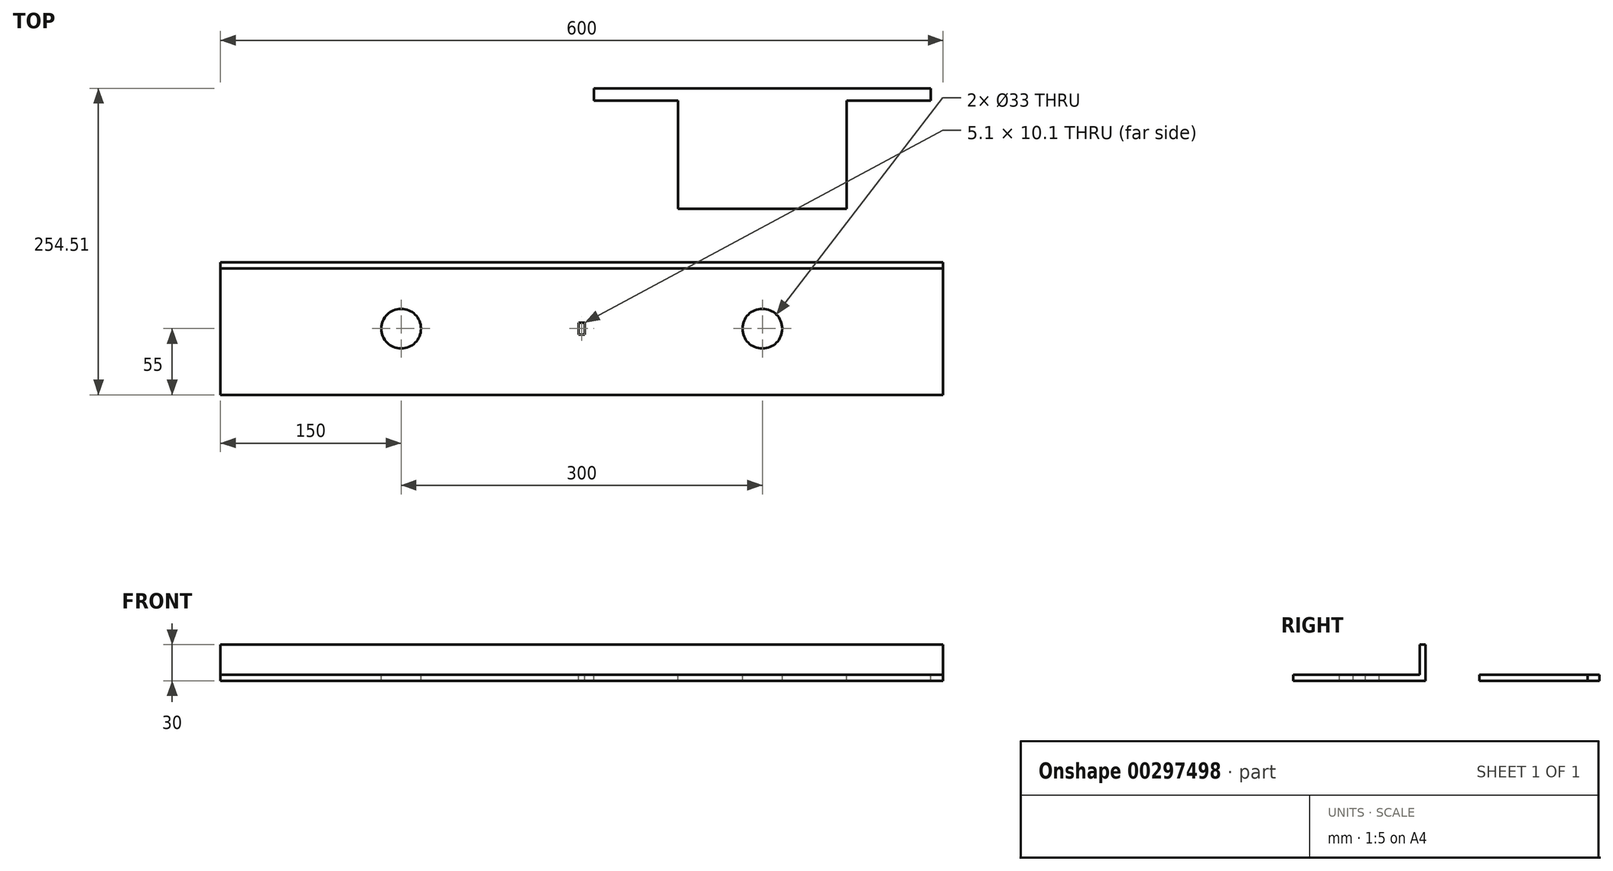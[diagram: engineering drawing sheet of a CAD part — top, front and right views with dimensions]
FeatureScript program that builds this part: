
annotation { "Feature Type Name" : "Feature", "Feature Type Description" : "" }
export const myFeature = defineFeature(function(context is Context, id is Id, definition is map)
    precondition{}
    {
        {
            var Q0;
            Q0=qCreatedBy(makeId("Top.planeOp"),FACE);
            var sketch = newSketch(context, id + "F0", { "sketchPlane" : qUnion([Q0])});
            skPoint(sketch, "E0", {"position": v(0, -50) * mm});
            skLineSegment(sketch, "E1.bottom", {"start": v(2.55, -55.05) * mm, "end": v(-2.55, -55.05) * mm});
            skLineSegment(sketch, "E1.top", {"start": v(2.55, -44.95) * mm, "end": v(-2.55, -44.95) * mm});
            skLineSegment(sketch, "E1.left", {"start": v(2.55, -55.05) * mm, "end": v(2.55, -44.95) * mm});
            skLineSegment(sketch, "E1.right", {"start": v(-2.55, -55.05) * mm, "end": v(-2.55, -44.95) * mm});
            skLineSegment(sketch, "E2.bottom", {"start": v(-300, 5) * mm, "end": v(300, 5) * mm});
            skLineSegment(sketch, "E2.top", {"start": v(-300, -105) * mm, "end": v(300, -105) * mm});
            skLineSegment(sketch, "E2.left", {"start": v(-300, 5) * mm, "end": v(-300, -105) * mm});
            skLineSegment(sketch, "E2.right", {"start": v(300, 5) * mm, "end": v(300, -105) * mm});
            skCircle(sketch, "E3", {"center": v(150, -50) * mm, "radius": 16.5 * mm});
            skCircle(sketch, "E4", {"center": v(-150, -50) * mm, "radius": 16.5 * mm});
            skLineSegment(sketch, "E5.top", {"start": v(-300, 0) * mm, "end": v(300, 0) * mm});
            skLineSegment(sketch, "E5.left", {"start": v(-300, 5) * mm, "end": v(-300, 0) * mm});
            skLineSegment(sketch, "E5.right", {"start": v(300, 5) * mm, "end": v(300, 0) * mm});
            skLineSegment(sketch, "E6", {"start": v(10, 149.51) * mm, "end": v(290, 149.51) * mm});
            skLineSegment(sketch, "E7", {"start": v(290, 139.51) * mm, "end": v(220, 139.51) * mm});
            skLineSegment(sketch, "E8", {"start": v(220, 139.51) * mm, "end": v(220, 49.51) * mm});
            skLineSegment(sketch, "E9", {"start": v(220, 49.51) * mm, "end": v(80, 49.51) * mm});
            skLineSegment(sketch, "E10", {"start": v(80, 49.51) * mm, "end": v(80, 139.51) * mm});
            skLineSegment(sketch, "E11", {"start": v(80, 139.51) * mm, "end": v(10, 139.51) * mm});
            skLineSegment(sketch, "E12", {"start": v(10, 139.51) * mm, "end": v(10, 149.51) * mm});
            skPoint(sketch, "E13", {"position": v(0, 99.51) * mm});
            skLineSegment(sketch, "E14", {"start": v(290, 149.51) * mm, "end": v(290, 139.51) * mm});
            skSolve(sketch);
        }
        {
            var Q0;
            Q0=makeQuery(id+"F0.imprint","IMPRINT",FACE,{"disambiguationData":[TD([[makeQuery(id+"F0.imprint","IMPRINT",EDGE,{"derivedFrom":sQuery(id+"F0.wireOp",EDGE,"E2.bottom")}),-1.0]])]});
            extrude(context, id + "F1", {"entities" : qUnion([Q0]), "depth" : 25 * mm});
        }
        {
            var Q0;
            Q0 = qSketchRegion(id + "F0", true);
            extrude(context, id + "F2", {"entities" : qUnion([Q0]), "operationType" : NewBodyOperationType.ADD, "oppositeDirection" : true, "depth" : 5 * mm});
        }
    });
